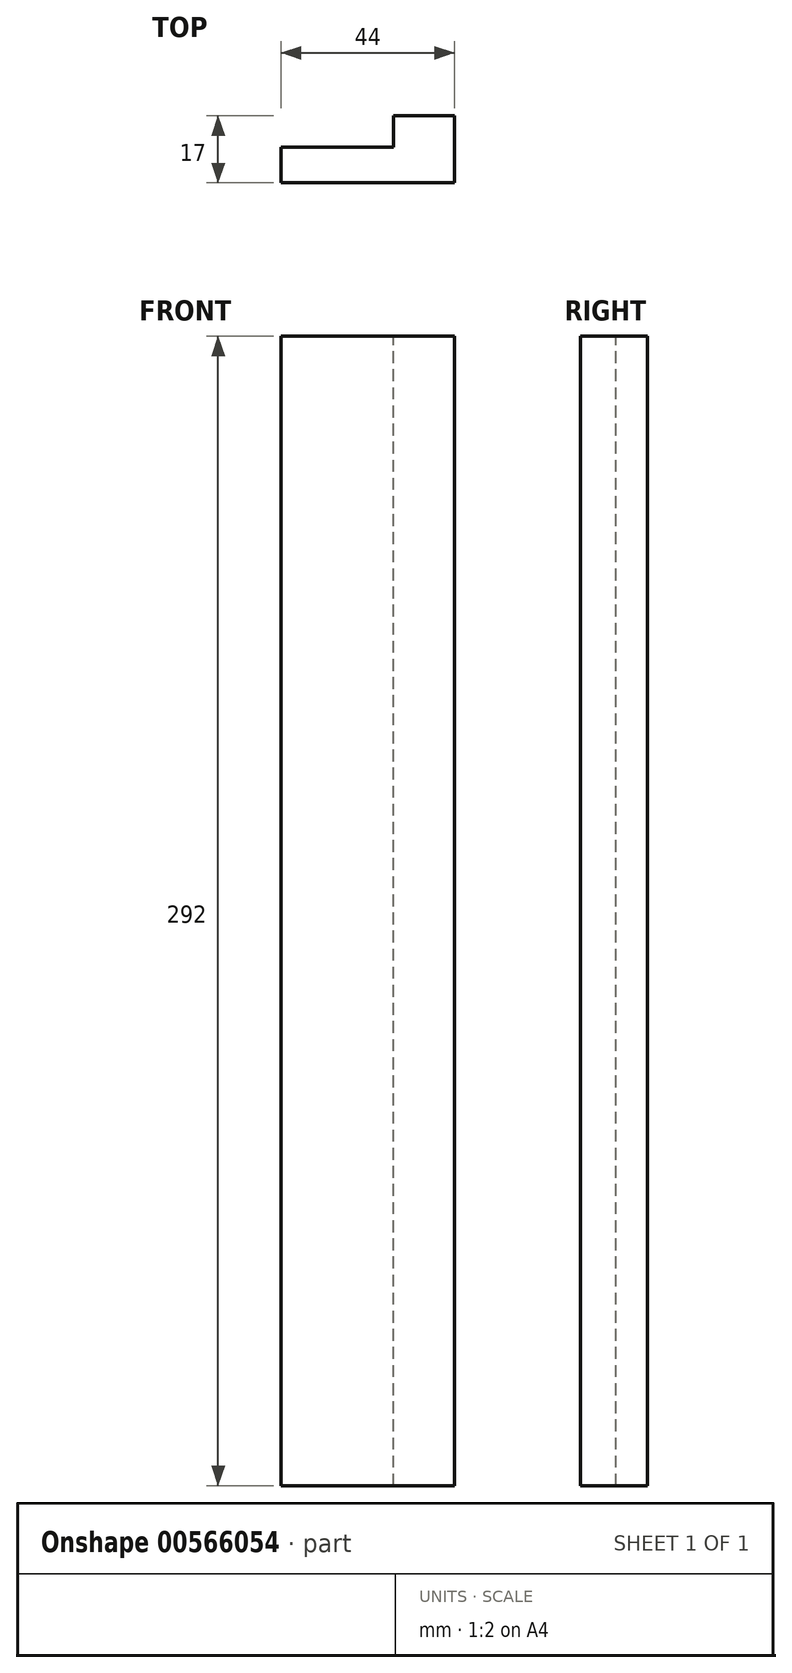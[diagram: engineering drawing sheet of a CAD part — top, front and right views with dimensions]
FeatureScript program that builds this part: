
annotation { "Feature Type Name" : "Feature", "Feature Type Description" : "" }
export const myFeature = defineFeature(function(context is Context, id is Id, definition is map)
    precondition{}
    {
        {
            var Q0;
            Q0=qCreatedBy(makeId("Front.planeOp"),FACE);
            var sketch = newSketch(context, id + "F0", { "sketchPlane" : qUnion([Q0])});
            skLineSegment(sketch, "E0.bottom", {"start": v(36.71, 217.99) * mm, "end": v(80.71, 217.99) * mm});
            skLineSegment(sketch, "E0.top", {"start": v(36.71, -74.01) * mm, "end": v(80.71, -74.01) * mm});
            skLineSegment(sketch, "E0.left", {"start": v(36.71, 217.99) * mm, "end": v(36.71, -74.01) * mm});
            skLineSegment(sketch, "E0.right", {"start": v(80.71, 217.99) * mm, "end": v(80.71, -74.01) * mm});
            skSolve(sketch);
        }
        {
            var Q0;
            Q0=qSketchRegion(id+"F0",true);
            extrude(context, id + "F1", {"entities" : qUnion([Q0]), "depth" : 17 * mm, "offsetDistance" : 25 * mm});
        }
        {
            var Q0;
            Q0=makeQuery(id+"F1.opExtrude","SWEPT_FACE",FACE,{"disambiguationData":[OSD([sQuery(id+"F0.wireOp",EDGE,"E0.bottom")])]});
            var sketch = newSketch(context, id + "F2", { "sketchPlane" : qUnion([Q0])});
            skLineSegment(sketch, "E1.right", {"start": v(65.21, 0) * mm, "end": v(65.21, -8) * mm});
            skLineSegment(sketch, "E2.bottom", {"start": v(36.71, 0) * mm, "end": v(65.21, 0) * mm});
            skLineSegment(sketch, "E2.top", {"start": v(36.71, -8) * mm, "end": v(65.21, -8) * mm});
            skLineSegment(sketch, "E2.left", {"start": v(36.71, 0) * mm, "end": v(36.71, -8) * mm});
            skSolve(sketch);
        }
        {
            var Q0;
            Q0=qSketchRegion(id+"F2",true);
            extrude(context, id + "F3", {"entities" : qUnion([Q0]), "operationType" : NewBodyOperationType.REMOVE, "oppositeDirection" : true, "depth" : 292 * mm, "offsetDistance" : 25 * mm});
        }
    });
